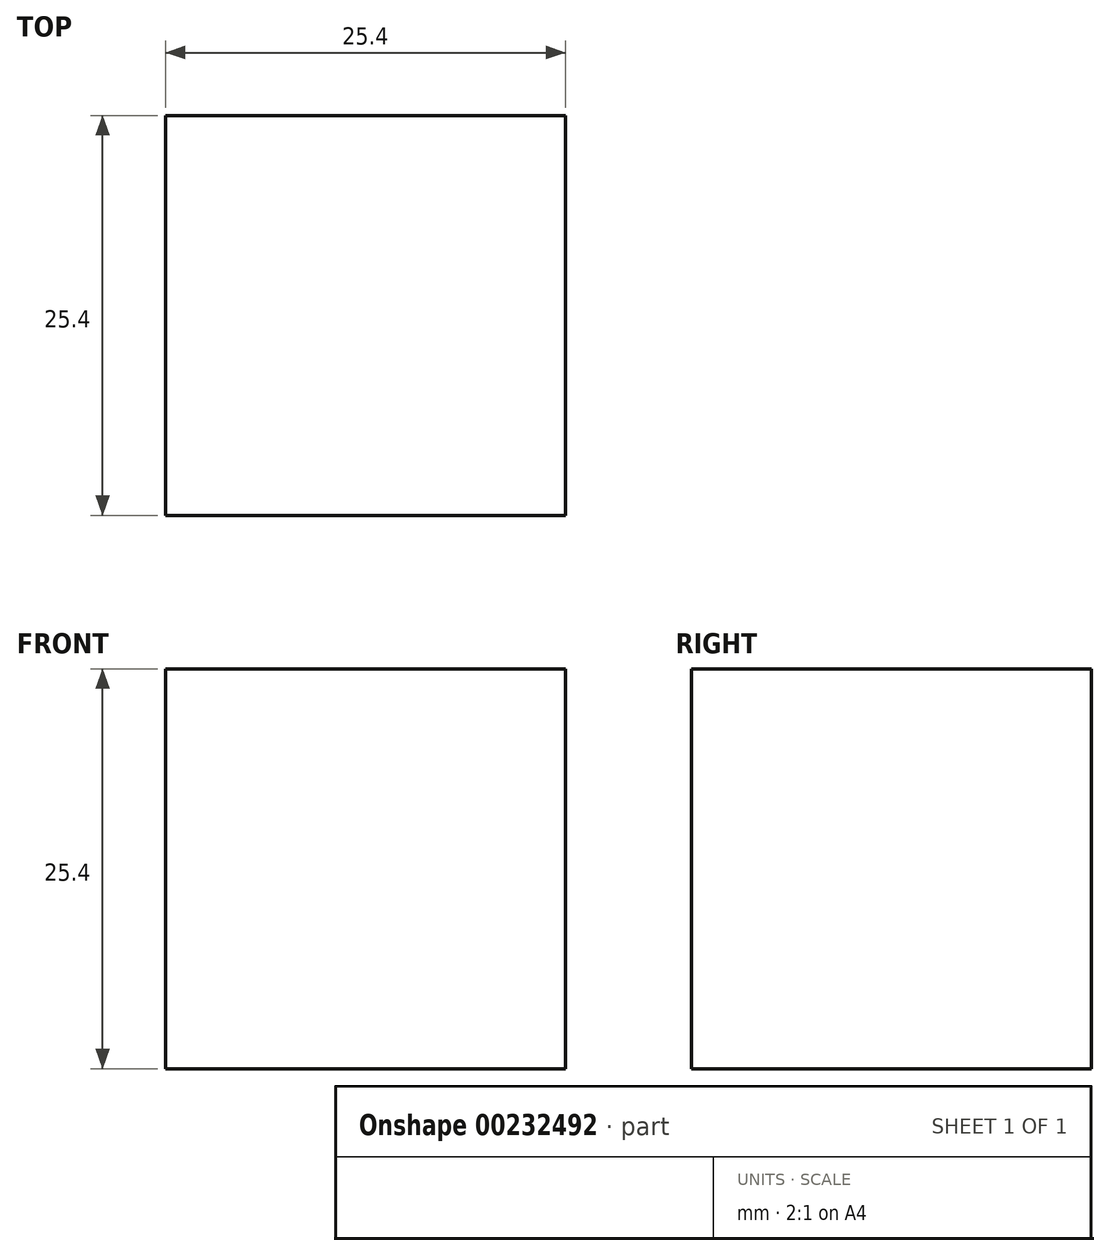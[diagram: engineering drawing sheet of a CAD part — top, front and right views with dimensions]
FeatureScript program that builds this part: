
annotation { "Feature Type Name" : "Feature", "Feature Type Description" : "" }
export const myFeature = defineFeature(function(context is Context, id is Id, definition is map)
    precondition{}
    {
        {
            var Q0;
            Q0=qCreatedBy(makeId("Top.planeOp"),FACE);
            var sketch = newSketch(context, id + "F0", { "sketchPlane" : qUnion([Q0])});
            skLineSegment(sketch, "E0.bottom", {"start": v(-18.78, 31.14) * mm, "end": v(6.62, 31.14) * mm});
            skLineSegment(sketch, "E0.top", {"start": v(-18.78, 5.74) * mm, "end": v(6.62, 5.74) * mm});
            skLineSegment(sketch, "E0.left", {"start": v(-18.78, 31.14) * mm, "end": v(-18.78, 5.74) * mm});
            skLineSegment(sketch, "E0.right", {"start": v(6.62, 31.14) * mm, "end": v(6.62, 5.74) * mm});
            skSolve(sketch);
        }
        {
            var Q0;
            Q0=makeQuery(id+"F0.imprint","IMPRINT",FACE,{"disambiguationData":[TD([[makeQuery(id+"F0.imprint","IMPRINT",EDGE,{"derivedFrom":sQuery(id+"F0.wireOp",EDGE,"E0.bottom")}),-1.0]])]});
            extrude(context, id + "F1", {"entities" : qUnion([Q0]), "depth" : 25.4 * mm});
        }
    });
